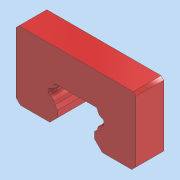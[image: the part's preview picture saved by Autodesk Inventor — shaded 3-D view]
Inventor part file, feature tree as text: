
AUTODESK INVENTOR PART (.ipt)
format: ipt  version: 2021 (Build 250183000, 183)  size: 156,160 bytes
history: native  units: mm
features: extrude x3, sketch x2, projected_geometry x1
ambient origin geometry x8: Origin, YZ Plane, XZ Plane, XY Plane, X Axis, Y Axis, Z Axis, Center Point
bodies: Solid1 (feature_tree)
feature tree (6):
  sketch  "Sketch1"  dims[d0=10.0mm d1=0.0mm d2=2.1mm d3=0.0mm]
  extrude  "Extrusion1"  Depth=2.1mm TaperAngle=0.0deg
  extrude  "Extrusion2"  [1 undecoded]
  extrude  "Extrusion3"  [1 undecoded]
  sketch  "Sketch2"  dims[d4=4.0mm d5=0.0mm]
  projected_geometry  "Projected Loop1"
note: 2 required parameter values undecoded (feature->parameter linkage not recoverable at this tier; creation-order binding heuristic only, values carry confidence <= 0.55)
